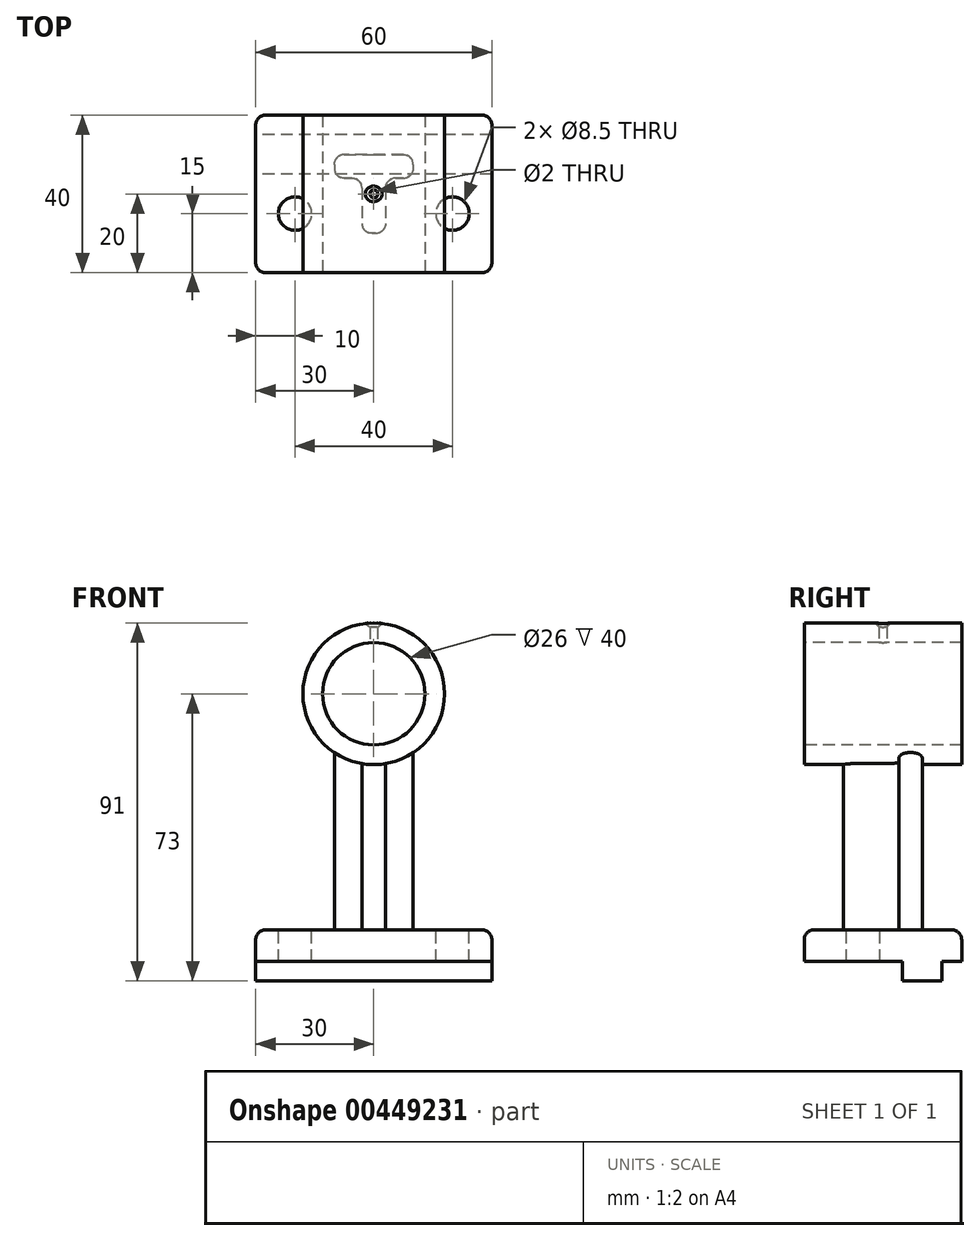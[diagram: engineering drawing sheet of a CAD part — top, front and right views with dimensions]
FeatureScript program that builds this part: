
annotation { "Feature Type Name" : "Feature", "Feature Type Description" : "" }
export const myFeature = defineFeature(function(context is Context, id is Id, definition is map)
    precondition{}
    {
        {
            var Q0;
            Q0=qCreatedBy(makeId("Front.planeOp"),FACE);
            var sketch = newSketch(context, id + "F0", { "sketchPlane" : qUnion([Q0])});
            skCircle(sketch, "E0", {"center": v(0, 0) * mm, "radius": 13 * mm});
            skCircle(sketch, "E1", {"center": v(0, 0) * mm, "radius": 18 * mm});
            skSolve(sketch);
        }
        {
            var Q0;
            Q0=makeQuery(id+"F0.imprint","IMPRINT",FACE,{"disambiguationData":[TD([[makeQuery(id+"F0.imprint","IMPRINT",EDGE,{"derivedFrom":sQuery(id+"F0.wireOp",EDGE,"E0")}),-1.0]])]});
            extrude(context, id + "F1", {"entities" : qUnion([Q0]), "oppositeDirection" : true, "depth" : 40 * mm});
        }
        {
            var Q0;
            Q0=qCreatedBy(makeId("Right.planeOp"),FACE);
            var sketch = newSketch(context, id + "F2", { "sketchPlane" : qUnion([Q0])});
            skLineSegment(sketch, "E2.bottom", {"start": v(0, -60) * mm, "end": v(40, -60) * mm});
            skLineSegment(sketch, "E2.top", {"start": v(0, -68) * mm, "end": v(40, -68) * mm});
            skLineSegment(sketch, "E2.left", {"start": v(0, -60) * mm, "end": v(0, -68) * mm});
            skLineSegment(sketch, "E2.right", {"start": v(40, -60) * mm, "end": v(40, -68) * mm});
            skLineSegment(sketch, "E3.bottom", {"start": v(35, -73) * mm, "end": v(25, -73) * mm});
            skLineSegment(sketch, "E3.top", {"start": v(35, -68) * mm, "end": v(25, -68) * mm});
            skLineSegment(sketch, "E3.left", {"start": v(35, -73) * mm, "end": v(35, -68) * mm});
            skLineSegment(sketch, "E3.right", {"start": v(25, -73) * mm, "end": v(25, -68) * mm});
            skSolve(sketch);
        }
        {
            var Q0;
            Q0 = qSketchRegion(id + "F2", true);
            extrude(context, id + "F3", {"entities" : qUnion([Q0]), "depth" : 60 * mm, "symmetric" : true});
        }
        {
            var Q0;
            Q0=makeQuery(id+"F3.opExtrude","SWEPT_FACE",FACE,{"disambiguationData":[OSD([sQuery(id+"F2.wireOp",EDGE,"E2.bottom")])]});
            var sketch = newSketch(context, id + "F4", { "sketchPlane" : qUnion([Q0])});
            skLineSegment(sketch, "E4", {"start": v(0, 0) * mm, "end": v(0, 39.5) * mm, "construction": true});
            skLineSegment(sketch, "E5", {"start": v(0, 15) * mm, "end": v(-20, 15) * mm, "construction": true});
            skPoint(sketch, "E6", {"position": v(-20, 15) * mm});
            skPoint(sketch, "E7.MirrorP", {"position": v(20, 15) * mm});
            skLineSegment(sketch, "E8.bottom", {"start": v(7.5, 30) * mm, "end": v(-7.5, 30) * mm});
            skLineSegment(sketch, "E8.top", {"start": v(7.5, 24) * mm, "end": v(5.5, 24) * mm});
            skLineSegment(sketch, "E8.left", {"start": v(10, 27.5) * mm, "end": v(10, 26.5) * mm});
            skLineSegment(sketch, "E8.right", {"start": v(-10, 27.5) * mm, "end": v(-10, 26.5) * mm});
            skPoint(sketch, "E8.middle", {"position": v(0, 27) * mm});
            skLineSegment(sketch, "E9.bottom", {"start": v(0, 30) * mm, "end": v(-3, 30) * mm});
            skLineSegment(sketch, "E9.top", {"start": v(0.5, 10) * mm, "end": v(-0.5, 10) * mm});
            skLineSegment(sketch, "E9.left", {"start": v(3, 21.5) * mm, "end": v(3, 12.5) * mm});
            skLineSegment(sketch, "E9.right", {"start": v(-3, 21.5) * mm, "end": v(-3, 12.5) * mm});
            skPoint(sketch, "E9.middle", {"position": v(0, 20) * mm});
            skLineSegment(sketch, "E10.trimOffspring", {"start": v(-5.5, 24) * mm, "end": v(-7.5, 24) * mm});
            skPoint(sketch, "E11.orphan", {"position": v(3, 30) * mm});
            skPoint(sketch, "E12.visualSharp", {"position": v(-10, 30) * mm});
            skArc(sketch, "E12.filletArc", {"start": v(-7.5, 30) * mm, "mid": v(-9.27, 29.27) * mm, "end": v(-10, 27.5) * mm});
            skPoint(sketch, "E13.visualSharp", {"position": v(10, 30) * mm});
            skArc(sketch, "E13.filletArc", {"start": v(10, 27.5) * mm, "mid": v(9.27, 29.27) * mm, "end": v(7.5, 30) * mm});
            skPoint(sketch, "E14.visualSharp", {"position": v(10, 24) * mm});
            skArc(sketch, "E14.filletArc", {"start": v(7.5, 24) * mm, "mid": v(9.27, 24.73) * mm, "end": v(10, 26.5) * mm});
            skPoint(sketch, "E15.visualSharp", {"position": v(3, 24) * mm});
            skArc(sketch, "E15.filletArc", {"start": v(5.5, 24) * mm, "mid": v(3.73, 23.27) * mm, "end": v(3, 21.5) * mm});
            skPoint(sketch, "E16.visualSharp", {"position": v(-3, 24) * mm});
            skArc(sketch, "E16.filletArc", {"start": v(-3, 21.5) * mm, "mid": v(-3.73, 23.27) * mm, "end": v(-5.5, 24) * mm});
            skPoint(sketch, "E17.visualSharp", {"position": v(-10, 24) * mm});
            skArc(sketch, "E17.filletArc", {"start": v(-10, 26.5) * mm, "mid": v(-9.27, 24.73) * mm, "end": v(-7.5, 24) * mm});
            skPoint(sketch, "E18.visualSharp", {"position": v(-3, 10) * mm});
            skArc(sketch, "E18.filletArc", {"start": v(-3, 12.5) * mm, "mid": v(-2.27, 10.73) * mm, "end": v(-0.5, 10) * mm});
            skPoint(sketch, "E19.visualSharp", {"position": v(3, 10) * mm});
            skArc(sketch, "E19.filletArc", {"start": v(0.5, 10) * mm, "mid": v(2.27, 10.73) * mm, "end": v(3, 12.5) * mm});
            skSolve(sketch);
        }
        {
            var Q0;
            Q0 = qSketchRegion(id + "F4", true);
            extrude(context, id + "F5", {"entities" : qUnion([Q0]), "operationType" : NewBodyOperationType.ADD, "endBound" : BoundingType.UP_TO_NEXT, "depth" : 25 * mm});
        }
        {
            var Q0;
            Q0=sQuery(id+"F4.wireOp",VERTEX,"E6");
            var Q1;
            Q1=sQuery(id+"F4.wireOp",VERTEX,"E7.MirrorP");
            var Q2;
            Q2=makeQuery(id+"F1.opExtrude","SWEPT_BODY",BODY,{"disambiguationData":[OSD([sQuery(id+"F0.wireOp",EDGE,"E0"),sQuery(id+"F0.wireOp",EDGE,"E1")])]});
            hole(context, id + "F6", {"style" : HoleStyle.SIMPLE, "endStyle" : HoleEndStyle.THROUGH, "holeDiameter" : 8.5 * mm, "tappedDepth" : 12 * mm, "tapClearance" : 3, "startFromSketch" : true, "locations" : qUnion([Q0, Q1]), "scope" : qUnion([Q2])});
        }
        {
            var Q0;
            Q0=qCreatedBy(makeId("Top.planeOp"),FACE);
            var sketch = newSketch(context, id + "F7", { "sketchPlane" : qUnion([Q0])});
            skCircle(sketch, "E20", {"center": v(0, 20) * mm, "radius": 1 * mm});
            skSolve(sketch);
        }
        {
            var Q0;
            Q0 = qSketchRegion(id + "F7", true);
            extrude(context, id + "F8", {"entities" : qUnion([Q0]), "operationType" : NewBodyOperationType.REMOVE, "endBound" : BoundingType.THROUGH_ALL, "depth" : 25 * mm});
        }
        {
            var Q0;
            Q0=makeQuery(id+"F8.boolean.opBoolean","INTERSECT",EDGE,{"derivedFrom":[makeQuery(id+"F1.opExtrude","SWEPT_FACE",FACE,{"disambiguationData":[OSD([sQuery(id+"F0.wireOp",EDGE,"E1")])]}),makeQuery(id+"F8.opExtrude","SWEPT_FACE",FACE,{"disambiguationData":[OSD([sQuery(id+"F7.wireOp",EDGE,"E20")])]})]});
            chamfer(context, id + "F9", {"entities" : qUnion([Q0]), "width" : 1 * mm, "tangentPropagation" : true});
        }
        {
            var Q0;
            Q0=makeQuery(id+"F3.opExtrude","CAP_EDGE",EDGE,{"disambiguationData":[OSD([sQuery(id+"F2.wireOp",EDGE,"E2.left")])],"isStart":false});
            var Q1;
            Q1=makeQuery(id+"F3.opExtrude","CAP_EDGE",EDGE,{"disambiguationData":[OSD([sQuery(id+"F2.wireOp",EDGE,"E2.left")])],"isStart":true});
            var Q2;
            Q2=makeQuery(id+"F3.opExtrude","CAP_EDGE",EDGE,{"disambiguationData":[OSD([sQuery(id+"F2.wireOp",EDGE,"E2.right")])],"isStart":false});
            var Q3;
            Q3=makeQuery(id+"F3.opExtrude","CAP_EDGE",EDGE,{"disambiguationData":[OSD([sQuery(id+"F2.wireOp",EDGE,"E2.right")])],"isStart":true});
            var Q4;
            Q4=makeQuery(id+"F5.opExtrude","CAP_EDGE",EDGE,{"disambiguationData":[OSD([sQuery(id+"F4.wireOp",EDGE,"E9.left")])],"isStart":true});
            var Q5;
            Q5=makeQuery(id+"F5.opExtrude","CAP_EDGE",EDGE,{"disambiguationData":[OSD([sQuery(id+"F4.wireOp",EDGE,"E9.left")])],"isStart":false});
            fillet(context, id + "F10", {"entities" : qUnion([Q0, Q1, Q2, Q3, Q4, Q5]), "radius" : 2.5 * mm, "tangentPropagation" : true, "allowEdgeOverflow" : false});
        }
        {
            var Q0;
            Q0=makeQuery(id+"F3.opExtrude","SWEPT_EDGE",EDGE,{"disambiguationData":[OSD([sQuery(id+"F2.wireOp",EDGE,"E2.bottom"),sQuery(id+"F2.wireOp",EDGE,"E2.left")])]});
            fillet(context, id + "F11", {"entities" : qUnion([Q0]), "radius" : 2.5 * mm, "tangentPropagation" : true, "allowEdgeOverflow" : false});
        }
    });
